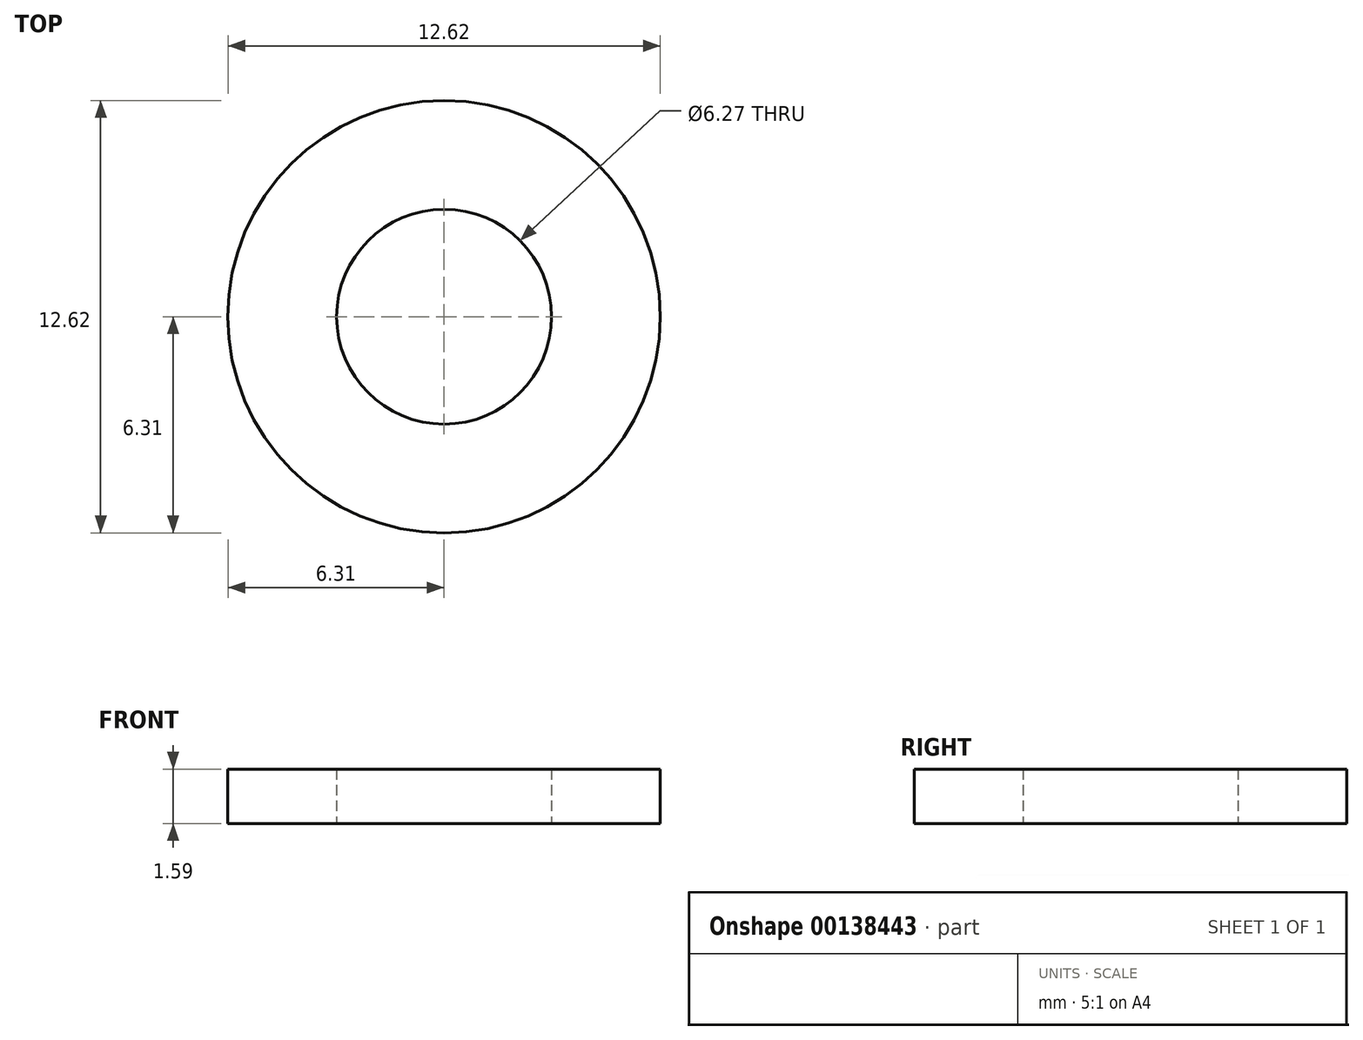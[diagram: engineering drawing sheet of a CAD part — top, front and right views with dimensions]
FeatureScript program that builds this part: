
annotation { "Feature Type Name" : "Feature", "Feature Type Description" : "" }
export const myFeature = defineFeature(function(context is Context, id is Id, definition is map)
    precondition{}
    {
        {
            var Q0;
            Q0=qCreatedBy(makeId("Top.planeOp"),FACE);
            var sketch = newSketch(context, id + "F0", { "sketchPlane" : qUnion([Q0])});
            skCircle(sketch, "E0", {"center": v(0, 0) * mm, "radius": 6.31 * mm});
            skCircle(sketch, "E1", {"center": v(0, 0) * mm, "radius": 3.14 * mm});
            skSolve(sketch);
        }
        {
            var Q0;
            Q0=qSketchRegion(id+"F0",true);
            extrude(context, id + "F1", {"entities" : qUnion([Q0]), "depth" : 1.59 * mm});
        }
    });
